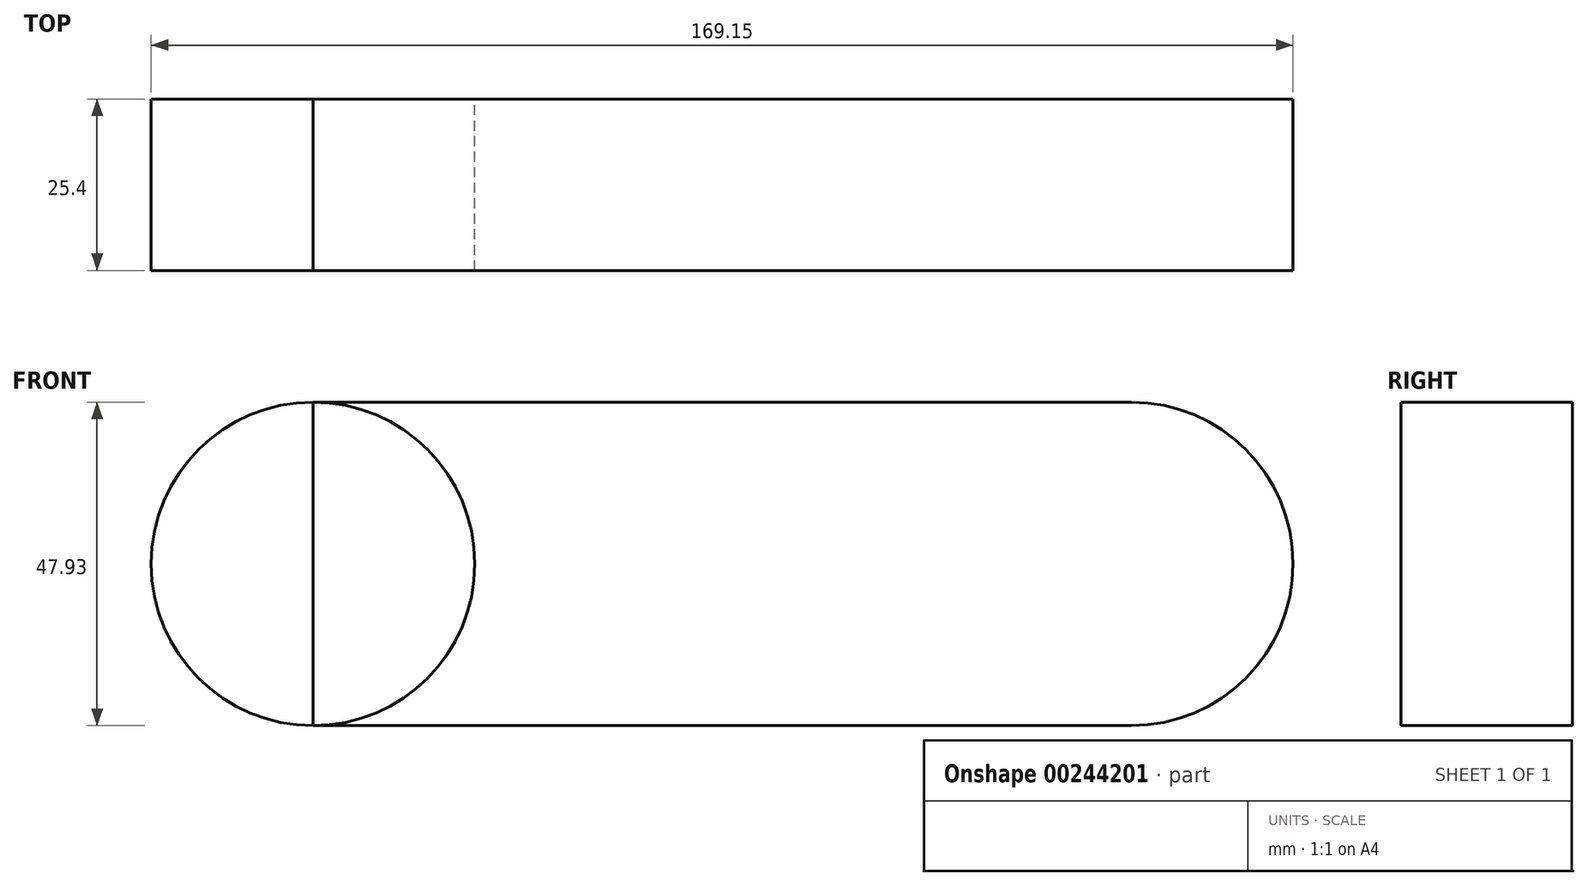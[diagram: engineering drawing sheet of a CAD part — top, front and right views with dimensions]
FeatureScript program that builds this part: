
annotation { "Feature Type Name" : "Feature", "Feature Type Description" : "" }
export const myFeature = defineFeature(function(context is Context, id is Id, definition is map)
    precondition{}
    {
        {
            var Q0;
            Q0=qCreatedBy(makeId("Front.planeOp"),FACE);
            var sketch = newSketch(context, id + "F1", { "sketchPlane" : qUnion([Q0])});
            skLineSegment(sketch, "E0.bottom", {"start": v(-59.07, -7.68) * mm, "end": v(62.15, -7.68) * mm});
            skLineSegment(sketch, "E0.top", {"start": v(-59.07, 40.25) * mm, "end": v(62.15, 40.25) * mm});
            skLineSegment(sketch, "E0.left", {"start": v(-59.07, -7.68) * mm, "end": v(-59.07, 40.25) * mm});
            skLineSegment(sketch, "E0.right", {"start": v(62.15, -7.68) * mm, "end": v(62.15, 40.25) * mm});
            skCircle(sketch, "E1", {"center": v(62.15, 16.29) * mm, "radius": 23.97 * mm});
            skCircle(sketch, "E2", {"center": v(-59.07, 16.29) * mm, "radius": 23.97 * mm});
            skSolve(sketch);
        }
        {
            var Q0;
            {var subQ0=sQuery(id+"F1.wireOp",EDGE,"E0.bottom");Q0=makeQuery(id+"F1.imprint","IMPRINT",FACE,{"disambiguationData":[TD([[makeQuery(id+"F1.imprint","IMPRINT",EDGE,{"derivedFrom":subQ0}),1.0]])]});}
            var Q1;
            {var subQ0=sQuery(id+"F1.wireOp",EDGE,"E0.right");Q1=makeQuery(id+"F1.imprint","IMPRINT",FACE,{"disambiguationData":[TD([[makeQuery(id+"F1.imprint","IMPRINT",EDGE,{"derivedFrom":subQ0}),1.0]])]});}
            var Q2;
            {var subQ0=sQuery(id+"F1.wireOp",EDGE,"E0.right");Q2=makeQuery(id+"F1.imprint","IMPRINT",FACE,{"disambiguationData":[TD([[makeQuery(id+"F1.imprint","IMPRINT",EDGE,{"derivedFrom":subQ0}),-1.0]])]});}
            var Q3;
            {var subQ0=sQuery(id+"F1.wireOp",EDGE,"E0.left");Q3=makeQuery(id+"F1.imprint","IMPRINT",FACE,{"disambiguationData":[TD([[makeQuery(id+"F1.imprint","IMPRINT",EDGE,{"derivedFrom":subQ0}),1.0]])]});}
            extrude(context, id + "F0", {"entities" : qUnion([Q0, Q1, Q2, Q3]), "depth" : 25.4 * mm});
        }
    });
